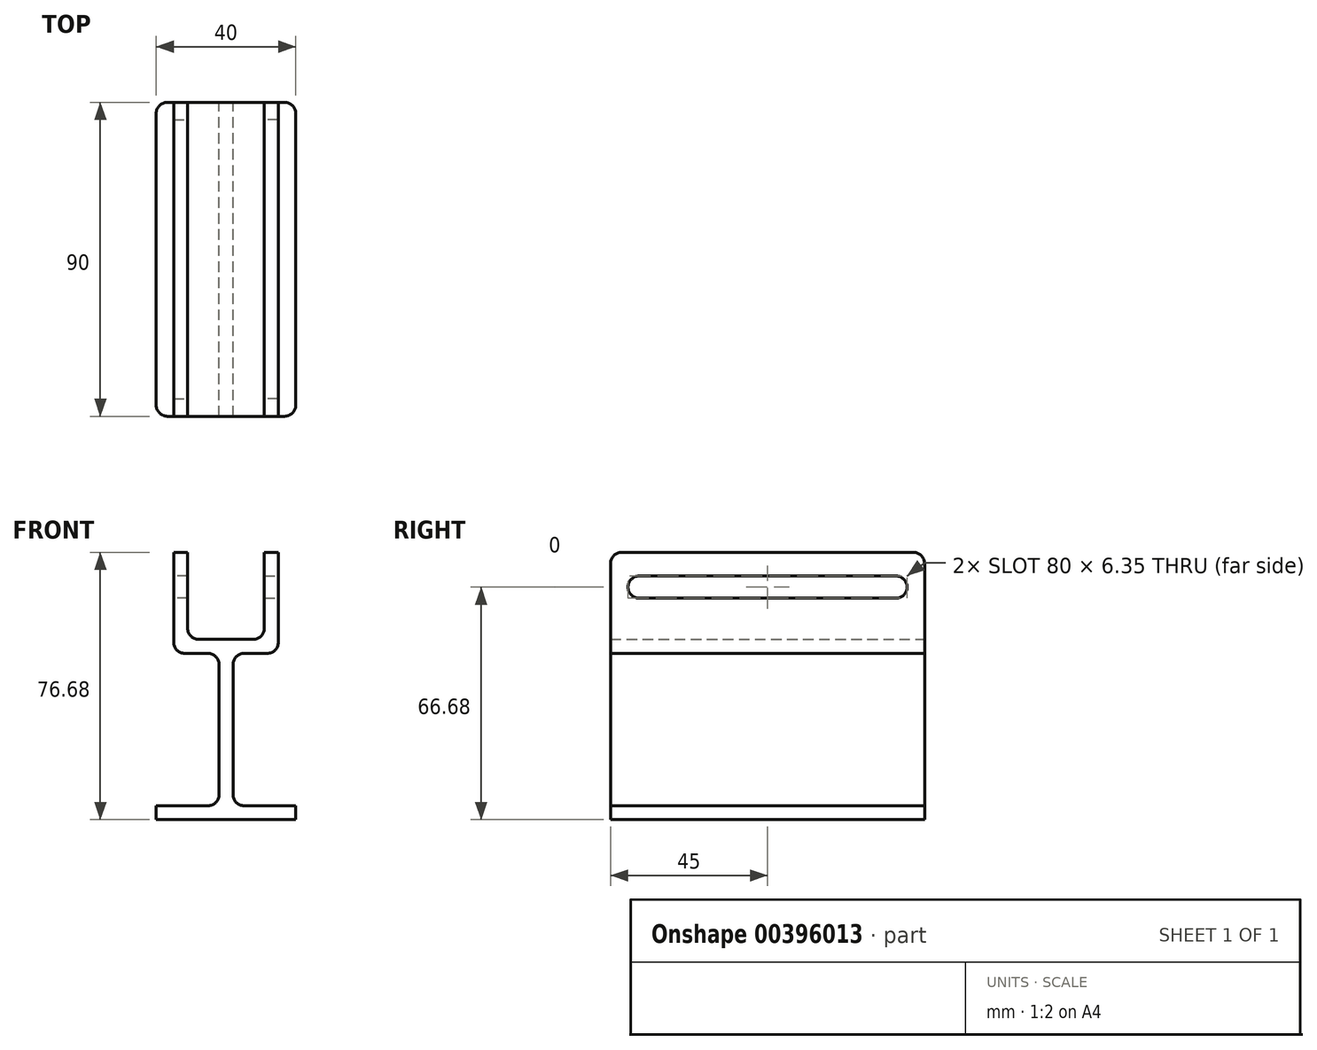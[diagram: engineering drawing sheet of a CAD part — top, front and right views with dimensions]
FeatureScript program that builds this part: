
annotation { "Feature Type Name" : "Feature", "Feature Type Description" : "" }
export const myFeature = defineFeature(function(context is Context, id is Id, definition is map)
    precondition{}
    {
        {
            var Q0;
            Q0=qCreatedBy(makeId("Front.planeOp"),FACE);
            var sketch = newSketch(context, id + "F0", { "sketchPlane" : qUnion([Q0])});
            skLineSegment(sketch, "E0", {"start": v(-15, 29) * mm, "end": v(-15, 0) * mm});
            skLineSegment(sketch, "E1", {"start": v(-15, 0) * mm, "end": v(-2, 0) * mm});
            skLineSegment(sketch, "E2", {"start": v(0, 0) * mm, "end": v(0, 4) * mm});
            skLineSegment(sketch, "E3", {"start": v(0, 4) * mm, "end": v(-11, 4) * mm});
            skLineSegment(sketch, "E4", {"start": v(-11, 4) * mm, "end": v(-11, 29) * mm});
            skLineSegment(sketch, "E5", {"start": v(-11, 29) * mm, "end": v(-15, 29) * mm});
            skLineSegment(sketch, "E6", {"start": v(-34.67, 19) * mm, "end": v(-5.49, 19) * mm});
            skLineSegment(sketch, "E7", {"start": v(-33.17, 25) * mm, "end": v(-6.65, 25) * mm});
            skLineSegment(sketch, "E8", {"start": v(-2, 0) * mm, "end": v(-2, -43.67) * mm});
            skLineSegment(sketch, "E9", {"start": v(-2, -43.67) * mm, "end": v(-20, -43.67) * mm});
            skLineSegment(sketch, "E10", {"start": v(-20, -43.67) * mm, "end": v(-20, -47.67) * mm});
            skLineSegment(sketch, "E11", {"start": v(-20, -47.67) * mm, "end": v(0, -47.67) * mm});
            skLineSegment(sketch, "E12", {"start": v(0, -47.67) * mm, "end": v(0, 0) * mm});
            skSolve(sketch);
        }
        {
            var Q0;
            Q0 = qSketchRegion(id + "F0", true);
            extrude(context, id + "F1", {"entities" : qUnion([Q0]), "depth" : 90 * mm, "offsetDistance" : 25 * mm});
        }
        {
            var Q0;
            Q0=makeQuery(id+"F1.opExtrude","SWEPT_FACE",FACE,{"disambiguationData":[OSD([sQuery(id+"F0.wireOp",EDGE,"E0")])]});
            var sketch = newSketch(context, id + "F2", { "sketchPlane" : qUnion([Q0])});
            skLineSegment(sketch, "E13.bottom", {"start": v(5, 22.18) * mm, "end": v(85, 22.18) * mm});
            skLineSegment(sketch, "E13.top", {"start": v(5, 15.83) * mm, "end": v(85, 15.83) * mm});
            skLineSegment(sketch, "E13.left", {"start": v(5, 22.18) * mm, "end": v(5, 15.83) * mm});
            skLineSegment(sketch, "E13.right", {"start": v(85, 22.18) * mm, "end": v(85, 15.83) * mm});
            skSolve(sketch);
        }
        {
            var Q0;
            Q0 = qSketchRegion(id + "F2", true);
            extrude(context, id + "F3", {"entities" : qUnion([Q0]), "operationType" : NewBodyOperationType.REMOVE, "oppositeDirection" : true, "depth" : 25 * mm, "offsetDistance" : 25 * mm});
        }
        {
            var Q0;
            Q0=makeQuery(id+"F1.opExtrude","CAP_EDGE",EDGE,{"disambiguationData":[OSD([sQuery(id+"F0.wireOp",EDGE,"E5")])],"isStart":true});
            var Q1;
            Q1=makeQuery(id+"F1.opExtrude","CAP_EDGE",EDGE,{"disambiguationData":[OSD([sQuery(id+"F0.wireOp",EDGE,"E5")])],"isStart":false});
            var Q2;
            Q2=makeQuery(id+"F1.opExtrude","SWEPT_EDGE",EDGE,{"disambiguationData":[OSD([sQuery(id+"F0.wireOp",EDGE,"E3"),sQuery(id+"F0.wireOp",EDGE,"E4")])]});
            var Q3;
            Q3=makeQuery(id+"F1.opExtrude","SWEPT_EDGE",EDGE,{"disambiguationData":[OSD([sQuery(id+"F0.wireOp",EDGE,"E0"),sQuery(id+"F0.wireOp",EDGE,"E1")])]});
            var Q4;
            Q4=makeQuery(id+"F1.opExtrude","CAP_EDGE",EDGE,{"disambiguationData":[OSD([sQuery(id+"F0.wireOp",EDGE,"E10")])],"isStart":true});
            var Q5;
            Q5=makeQuery(id+"F1.opExtrude","CAP_EDGE",EDGE,{"disambiguationData":[OSD([sQuery(id+"F0.wireOp",EDGE,"E10")])],"isStart":false});
            var Q6;
            Q6=makeQuery(id+"F3.boolean.opBoolean","COPY",EDGE,{"derivedFrom":makeQuery(id+"F3.opExtrude","SWEPT_EDGE",EDGE,{"disambiguationData":[OSD([sQuery(id+"F2.wireOp",EDGE,"E13.bottom"),sQuery(id+"F2.wireOp",EDGE,"E13.right")])]})});
            var Q7;
            Q7=makeQuery(id+"F3.boolean.opBoolean","COPY",EDGE,{"derivedFrom":makeQuery(id+"F3.opExtrude","SWEPT_EDGE",EDGE,{"disambiguationData":[OSD([sQuery(id+"F2.wireOp",EDGE,"E13.top"),sQuery(id+"F2.wireOp",EDGE,"E13.right")])]})});
            var Q8;
            Q8=makeQuery(id+"F3.boolean.opBoolean","COPY",EDGE,{"derivedFrom":makeQuery(id+"F3.opExtrude","SWEPT_EDGE",EDGE,{"disambiguationData":[OSD([sQuery(id+"F2.wireOp",EDGE,"E13.top"),sQuery(id+"F2.wireOp",EDGE,"E13.left")])]})});
            var Q9;
            Q9=makeQuery(id+"F3.boolean.opBoolean","COPY",EDGE,{"derivedFrom":makeQuery(id+"F3.opExtrude","SWEPT_EDGE",EDGE,{"disambiguationData":[OSD([sQuery(id+"F2.wireOp",EDGE,"E13.bottom"),sQuery(id+"F2.wireOp",EDGE,"E13.left")])]})});
            var Q10;
            Q10=makeQuery(id+"F1.opExtrude","SWEPT_EDGE",EDGE,{"disambiguationData":[OSD([sQuery(id+"F0.wireOp",EDGE,"E8"),sQuery(id+"F0.wireOp",EDGE,"E9")])]});
            var Q11;
            Q11=makeQuery(id+"F1.opExtrude","SWEPT_EDGE",EDGE,{"disambiguationData":[OSD([sQuery(id+"F0.wireOp",EDGE,"E1"),sQuery(id+"F0.wireOp",EDGE,"E8")])]});
            fillet(context, id + "F4", {"entities" : qUnion([Q0, Q1, Q2, Q3, Q4, Q5, Q6, Q7, Q8, Q9, Q10, Q11]), "tangentPropagation" : true, "radius" : (6.35 / 2) * mm, "defaultsChanged" : false, "vertexSettings" : [], "allowEdgeOverflow" : false});
        }
        {
            var Q0;
            Q0=makeQuery(id+"F1.opExtrude","SWEPT_BODY",BODY,{"disambiguationData":[OSD([sQuery(id+"F0.wireOp",EDGE,"E0"),sQuery(id+"F0.wireOp",EDGE,"E1"),sQuery(id+"F0.wireOp",EDGE,"E2"),sQuery(id+"F0.wireOp",EDGE,"E3"),sQuery(id+"F0.wireOp",EDGE,"E4"),sQuery(id+"F0.wireOp",EDGE,"E5"),sQuery(id+"F0.wireOp",EDGE,"E8"),sQuery(id+"F0.wireOp",EDGE,"E9"),sQuery(id+"F0.wireOp",EDGE,"E10"),sQuery(id+"F0.wireOp",EDGE,"E11"),sQuery(id+"F0.wireOp",EDGE,"E12")])]});
            var Q1;
            Q1=qCreatedBy(makeId("Right.planeOp"),FACE);
            mirror(context, id + "F5", {"operationType" : NewBodyOperationType.ADD, "entities" : qUnion([Q0]), "mirrorPlane" : qUnion([Q1])});
        }
    });
